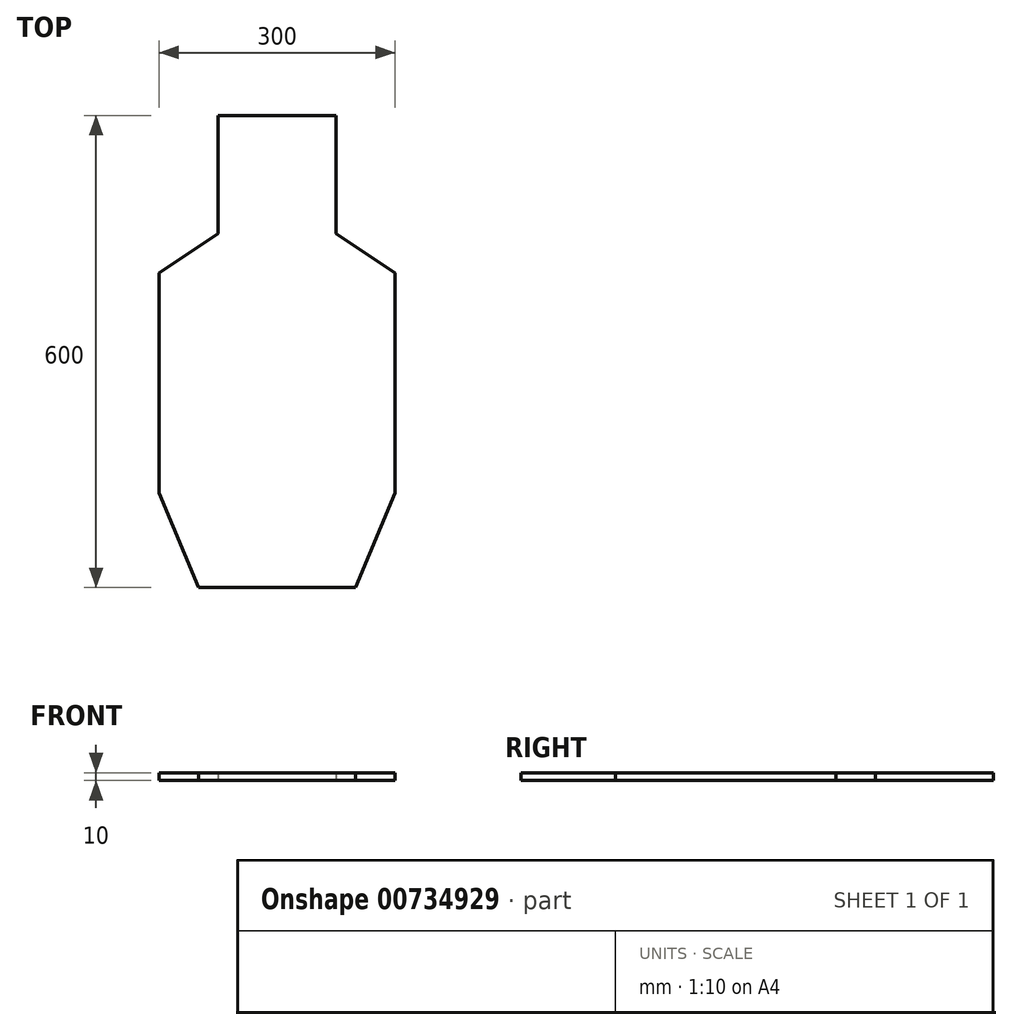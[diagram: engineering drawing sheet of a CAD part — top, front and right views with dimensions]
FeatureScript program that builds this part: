
annotation { "Feature Type Name" : "Feature", "Feature Type Description" : "" }
export const myFeature = defineFeature(function(context is Context, id is Id, definition is map)
    precondition{}
    {
        {
            var Q0;
            Q0=qCreatedBy(makeId("Top.planeOp"),FACE);
            var sketch = newSketch(context, id + "F0", { "sketchPlane" : qUnion([Q0])});
            skLineSegment(sketch, "E0", {"start": v(0, 156.98) * mm, "end": v(0, 436.98) * mm});
            skLineSegment(sketch, "E1", {"start": v(0, 436.98) * mm, "end": v(75, 486.98) * mm});
            skLineSegment(sketch, "E2", {"start": v(75, 486.98) * mm, "end": v(75, 636.98) * mm});
            skLineSegment(sketch, "E3", {"start": v(75, 636.98) * mm, "end": v(225, 636.98) * mm});
            skLineSegment(sketch, "E4", {"start": v(225, 636.98) * mm, "end": v(225, 486.98) * mm});
            skLineSegment(sketch, "E5", {"start": v(225, 486.98) * mm, "end": v(300, 436.98) * mm});
            skLineSegment(sketch, "E6", {"start": v(300, 436.98) * mm, "end": v(300, 156.98) * mm});
            skLineSegment(sketch, "E7", {"start": v(300, 156.98) * mm, "end": v(250, 36.98) * mm});
            skLineSegment(sketch, "E8", {"start": v(250, 36.98) * mm, "end": v(50, 36.98) * mm});
            skLineSegment(sketch, "E9", {"start": v(50, 36.98) * mm, "end": v(0, 156.98) * mm});
            skSolve(sketch);
        }
        {
            var Q0;
            Q0 = qSketchRegion(id + "F0", true);
            extrude(context, id + "F1", {"entities" : qUnion([Q0]), "depth" : 10 * mm, "offsetDistance" : 25 * mm});
        }
    });
